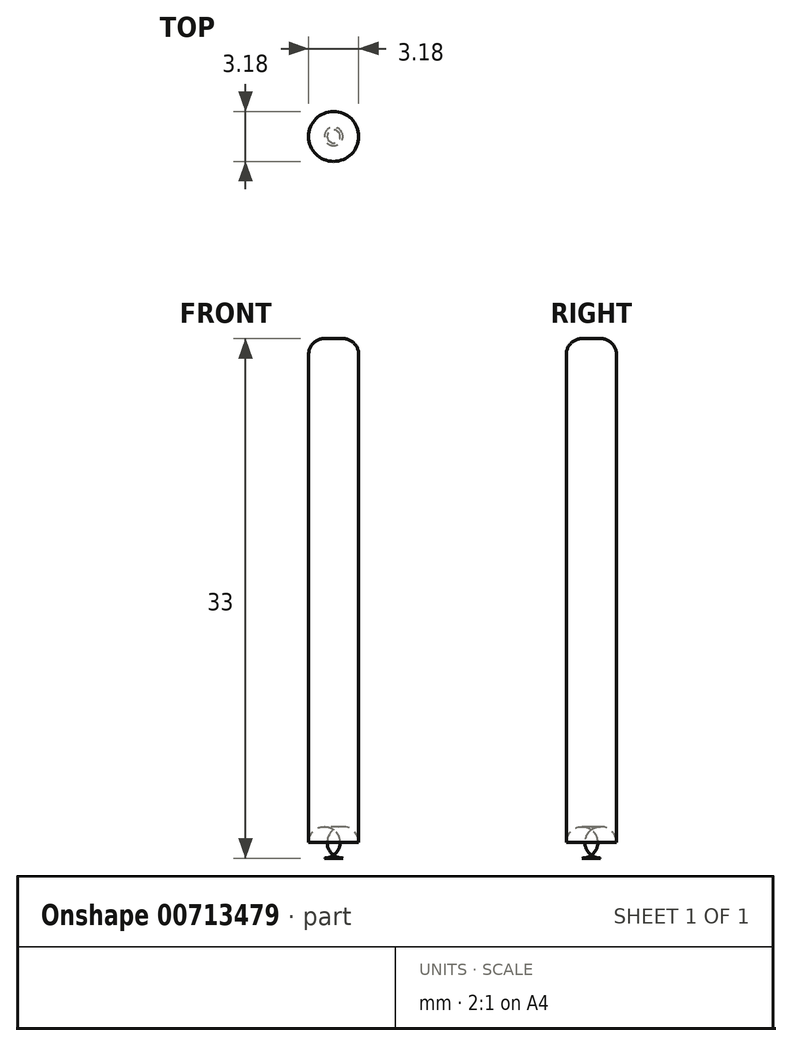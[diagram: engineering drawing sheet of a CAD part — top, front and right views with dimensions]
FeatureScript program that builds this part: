
annotation { "Feature Type Name" : "Feature", "Feature Type Description" : "" }
export const myFeature = defineFeature(function(context is Context, id is Id, definition is map)
    precondition{}
    {
        {
            assignVariable(context, id + "F0", {"name" : "length", "anyValue" : 33 * mm});
        }
        {
            var Q0;
            Q0=qCreatedBy(makeId("Top.planeOp"),FACE);
            var sketch = newSketch(context, id + "F1", { "sketchPlane" : qUnion([Q0])});
            skCircle(sketch, "E0", {"center": v(0, 0) * mm, "radius": 1.59 * mm});
            skSolve(sketch);
        }
        {
            var Q0;
            Q0=qSketchRegion(id+"F1",true);
            extrude(context, id + "F2", {"entities" : qUnion([Q0]), "depth" : getVariable(context, 'length'), "offsetDistance" : 25 * mm});
        }
        {
            var Q0;
            Q0=makeQuery(id+"F2.opExtrude","CAP_EDGE",EDGE,{"disambiguationData":[OSD([sQuery(id+"F1.wireOp",EDGE,"E0")])],"isStart":false});
            var Q1;
            Q1=makeQuery(id+"F2.opExtrude","CAP_EDGE",EDGE,{"disambiguationData":[OSD([sQuery(id+"F1.wireOp",EDGE,"E0")])],"isStart":true});
            fillet(context, id + "F3", {"entities" : qUnion([Q0, Q1]), "radius" : 1 * mm, "tangentPropagation" : true, "allowEdgeOverflow" : false});
        }
    });
